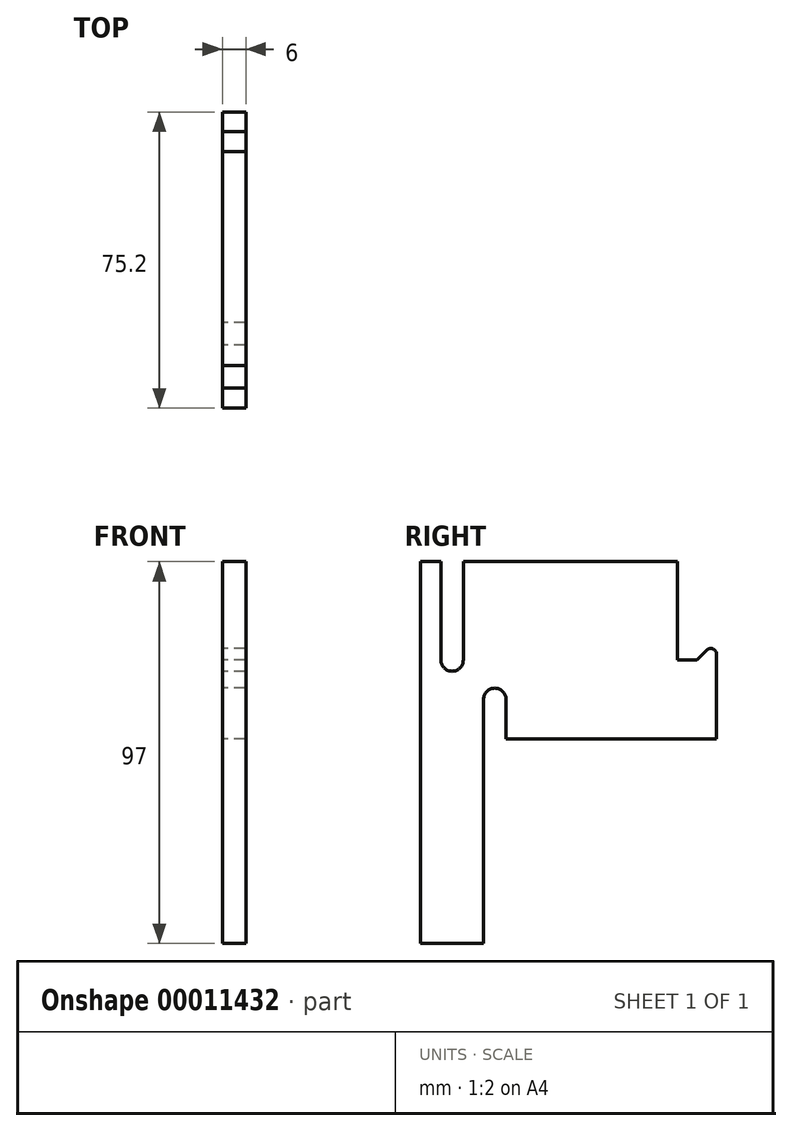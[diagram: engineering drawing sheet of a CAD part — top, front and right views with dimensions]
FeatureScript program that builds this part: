
annotation { "Feature Type Name" : "Feature", "Feature Type Description" : "" }
export const myFeature = defineFeature(function(context is Context, id is Id, definition is map)
    precondition{}
    {
        {
            var Q0;
            Q0=qCreatedBy(makeId("Right.planeOp"),FACE);
            var sketch = newSketch(context, id + "F0", { "sketchPlane" : qUnion([Q0])});
            skLineSegment(sketch, "E0.top", {"start": v(-16, 0) * mm, "end": v(0, 0) * mm});
            skLineSegment(sketch, "E0.left", {"start": v(-16, 62) * mm, "end": v(-16, 0) * mm});
            skLineSegment(sketch, "E0.right", {"start": v(0, 62) * mm, "end": v(0, 0) * mm});
            skLineSegment(sketch, "E1", {"start": v(-16, 97) * mm, "end": v(-10.85, 97) * mm});
            skLineSegment(sketch, "E2", {"start": v(0, 62) * mm, "end": v(5.7, 62) * mm, "construction": true});
            skLineSegment(sketch, "E3", {"start": v(5.7, 62) * mm, "end": v(5.7, 52) * mm});
            skLineSegment(sketch, "E4", {"start": v(5.7, 52) * mm, "end": v(59.2, 52) * mm});
            skLineSegment(sketch, "E5", {"start": v(59.2, 73.46) * mm, "end": v(59.2, 52) * mm});
            skLineSegment(sketch, "E6", {"start": v(49.2, 97) * mm, "end": v(49.2, 72) * mm});
            skLineSegment(sketch, "E7", {"start": v(49.2, 72) * mm, "end": v(54.2, 72) * mm});
            skLineSegment(sketch, "E8", {"start": v(-16, 97) * mm, "end": v(-16, 62) * mm});
            skLineSegment(sketch, "E9", {"start": v(-10.85, 97) * mm, "end": v(-10.85, 72) * mm});
            skLineSegment(sketch, "E10", {"start": v(-5.15, 72) * mm, "end": v(-5.15, 97) * mm});
            skLineSegment(sketch, "E11.trimOffspring", {"start": v(-5.15, 97) * mm, "end": v(49.2, 97) * mm});
            skLineSegment(sketch, "E12", {"start": v(-8, 97) * mm, "end": v(-8, 72) * mm, "construction": true});
            skLineSegment(sketch, "E13", {"start": v(54.2, 72) * mm, "end": v(56.7, 74.5) * mm});
            skArc(sketch, "E14", {"start": v(-10.85, 72) * mm, "mid": v(-8, 69.15) * mm, "end": v(-5.15, 72) * mm});
            skArc(sketch, "E15", {"start": v(5.7, 62) * mm, "mid": v(2.85, 64.85) * mm, "end": v(0, 62) * mm});
            skArc(sketch, "E16", {"start": v(59.2, 73.46) * mm, "mid": v(58.3, 74.82) * mm, "end": v(56.7, 74.5) * mm});
            skPoint(sketch, "E17.orphan", {"position": v(59.2, 77) * mm});
            skSolve(sketch);
        }
        {
            var Q0;
            Q0 = qSketchRegion(id + "F0", true);
            extrude(context, id + "F1", {"entities" : qUnion([Q0]), "depth" : 6 * mm});
        }
    });
